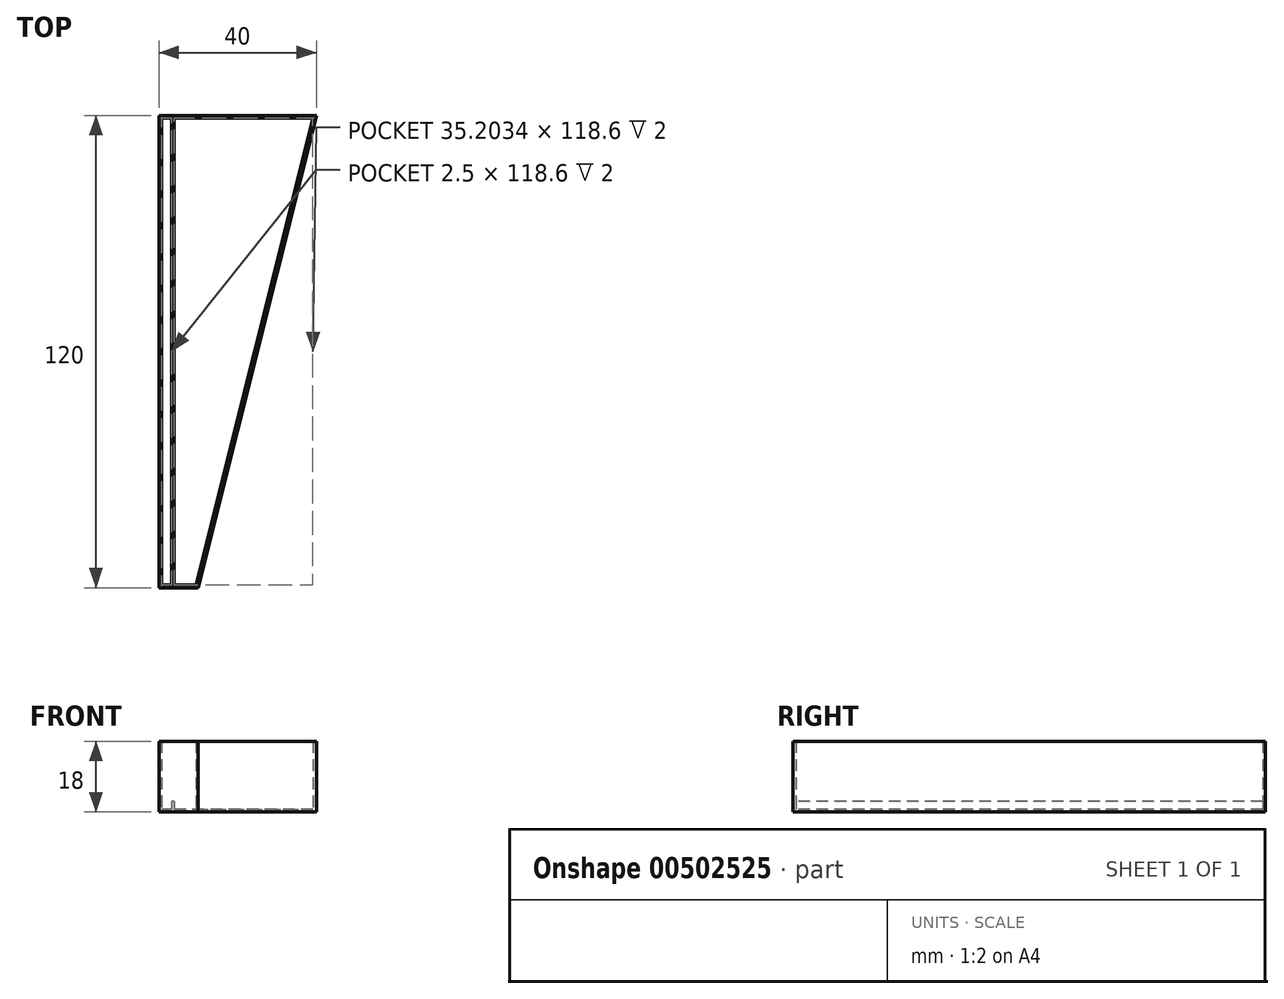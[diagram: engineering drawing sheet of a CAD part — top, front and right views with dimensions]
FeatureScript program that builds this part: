
annotation { "Feature Type Name" : "Feature", "Feature Type Description" : "" }
export const myFeature = defineFeature(function(context is Context, id is Id, definition is map)
    precondition{}
    {
        {
            var Q0;
            Q0=qCreatedBy(makeId("Top.planeOp"),FACE);
            var sketch = newSketch(context, id + "F0", { "sketchPlane" : qUnion([Q0])});
            skLineSegment(sketch, "E0", {"start": v(-2.41, 77.58) * mm, "end": v(-2.41, -42.42) * mm});
            skLineSegment(sketch, "E1", {"start": v(-2.41, -42.42) * mm, "end": v(7.59, -42.42) * mm});
            skLineSegment(sketch, "E2", {"start": v(7.59, -42.42) * mm, "end": v(37.59, 77.58) * mm});
            skLineSegment(sketch, "E3", {"start": v(37.59, 77.58) * mm, "end": v(-2.41, 77.58) * mm});
            skSolve(sketch);
        }
        {
            var Q0;
            Q0=makeQuery(id+"F0.imprint","IMPRINT",FACE,{"disambiguationData":[TD([[makeQuery(id+"F0.imprint","IMPRINT",EDGE,{"derivedFrom":sQuery(id+"F0.wireOp",EDGE,"E0")}),1.0]])]});
            extrude(context, id + "F1", {"entities" : qUnion([Q0]), "depth" : 18 * mm});
        }
        {
            var Q0;
            Q0=makeQuery(id+"F1.opExtrude","CAP_FACE",FACE,{"disambiguationData":[OSD([sQuery(id+"F0.wireOp",EDGE,"E0"),sQuery(id+"F0.wireOp",EDGE,"E1"),sQuery(id+"F0.wireOp",EDGE,"E2"),sQuery(id+"F0.wireOp",EDGE,"E3")])],"isStart":false});
            shell(context, id + "F2", {"entities" : qUnion([Q0]), "thickness" : 0.7 * mm});
        }
        {
            var Q0;
            Q0=makeQuery(id+"F2.opShell","OFFSET_FACE",FACE,{"disambiguationData":[OSD([sQuery(id+"F0.wireOp",EDGE,"E0"),sQuery(id+"F0.wireOp",EDGE,"E1"),sQuery(id+"F0.wireOp",EDGE,"E2"),sQuery(id+"F0.wireOp",EDGE,"E3")])]});
            var sketch = newSketch(context, id + "F3", { "sketchPlane" : qUnion([Q0])});
            skSolve(sketch);
        }
        {
            var Q0;
            {var subQ0=sQuery(id+"F0.wireOp",EDGE,"E0");Q0=makeQuery(id+"F3.imprint","IMPRINT",FACE,{"disambiguationData":[TD([[makeQuery(id+"F3.imprint","IMPRINT",EDGE,{"derivedFrom":makeQuery(id+"F2.opShell","OFFSET_EDGE",EDGE,{"disambiguationData":[OSD([subQ0]),TDD([makeQuery(id+"F1.opExtrude","CAP_EDGE",EDGE,{"disambiguationData":[OSD([subQ0])],"isStart":true})])]})}),1.0]])]});}
            var sketch = newSketch(context, id + "F4", { "sketchPlane" : qUnion([Q0])});
            skLineSegment(sketch, "E4.bottom", {"start": v(0, 76.88) * mm, "end": v(1.49, 76.88) * mm});
            skLineSegment(sketch, "E4.top", {"start": v(0.79, -41.72) * mm, "end": v(1.49, -41.72) * mm});
            skLineSegment(sketch, "E4.left", {"start": v(0.79, 76.88) * mm, "end": v(0.79, -41.72) * mm});
            skLineSegment(sketch, "E4.right", {"start": v(1.49, 76.88) * mm, "end": v(1.49, -41.72) * mm});
            skLineSegment(sketch, "E5.0", {"start": v(-1.71, -41.72) * mm, "end": v(7.04, -41.72) * mm});
            skLineSegment(sketch, "E6.0", {"start": v(36.69, 76.88) * mm, "end": v(-1.71, 76.88) * mm});
            skLineSegment(sketch, "E7", {"start": v(0.79, 76.88) * mm, "end": v(1.49, 76.88) * mm});
            skSolve(sketch);
        }
        {
            var Q0;
            Q0 = qSketchRegion(id + "F4", true);
            extrude(context, id + "F5", {"entities" : qUnion([Q0]), "operationType" : NewBodyOperationType.ADD, "depth" : 2 * mm, "offsetDistance" : 25 * mm});
        }
    });
